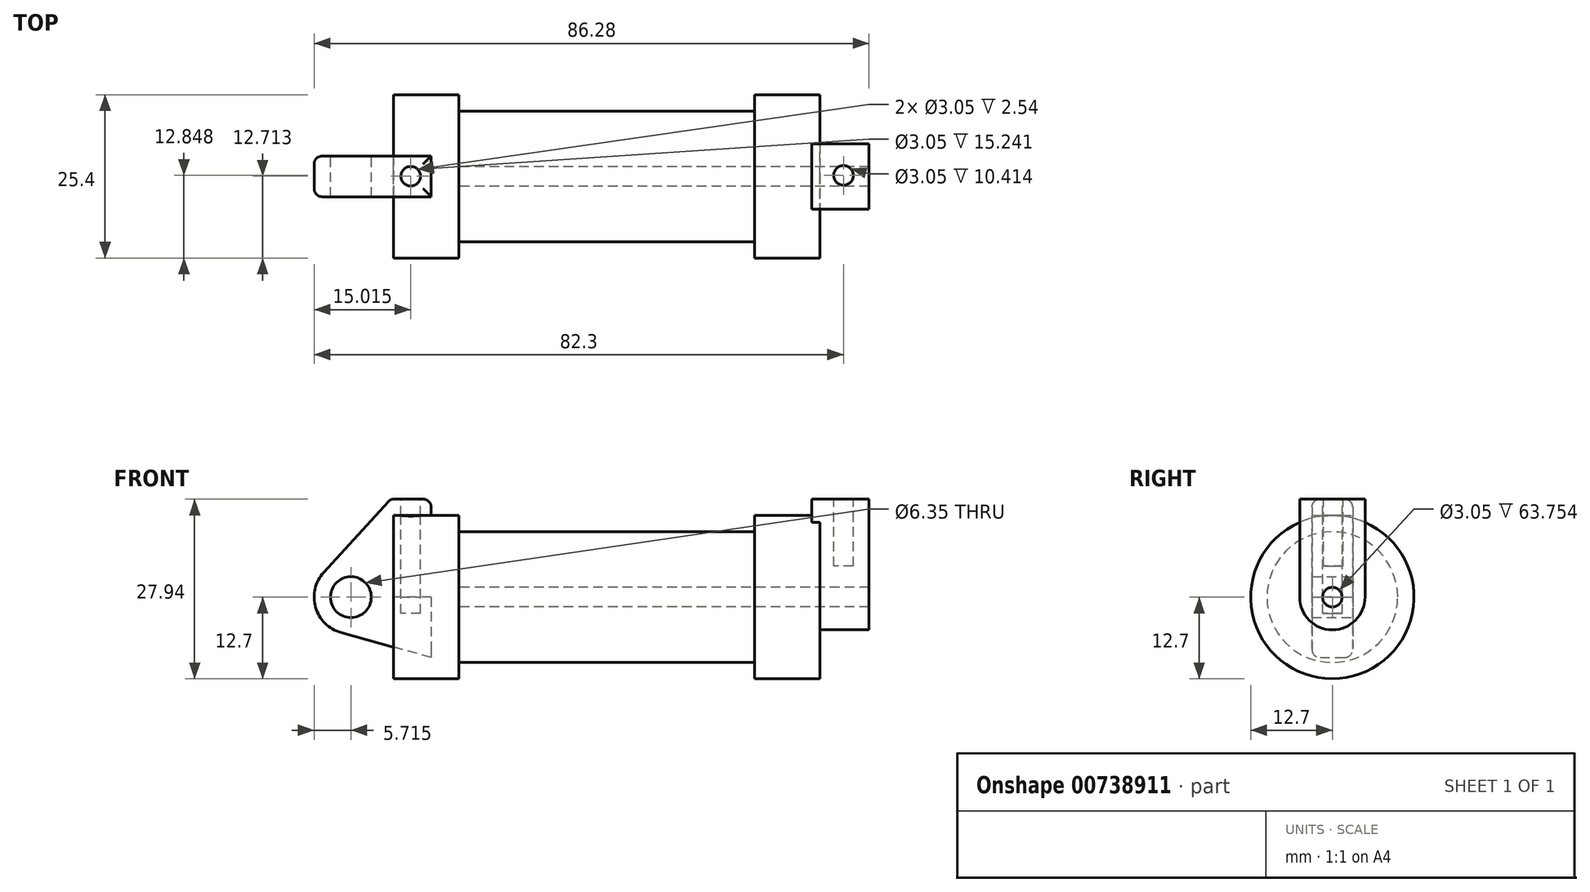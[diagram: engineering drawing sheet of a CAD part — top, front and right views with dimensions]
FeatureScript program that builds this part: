
annotation { "Feature Type Name" : "Feature", "Feature Type Description" : "" }
export const myFeature = defineFeature(function(context is Context, id is Id, definition is map)
    precondition{}
    {
        {
            var Q0;
            Q0=qCreatedBy(makeId("Front.planeOp"),FACE);
            var sketch = newSketch(context, id + "F0", { "sketchPlane" : qUnion([Q0])});
            skLineSegment(sketch, "E0", {"start": v(0, 0) * mm, "end": v(0, 12.7) * mm});
            skLineSegment(sketch, "E1", {"start": v(0, 12.7) * mm, "end": v(10.16, 12.7) * mm});
            skLineSegment(sketch, "E2", {"start": v(10.16, 12.7) * mm, "end": v(10.16, 10.16) * mm});
            skLineSegment(sketch, "E3", {"start": v(10.16, 10.16) * mm, "end": v(56.13, 10.16) * mm});
            skLineSegment(sketch, "E4", {"start": v(56.13, 10.16) * mm, "end": v(56.13, 12.7) * mm});
            skLineSegment(sketch, "E5", {"start": v(56.13, 12.7) * mm, "end": v(66.3, 12.7) * mm});
            skLineSegment(sketch, "E6", {"start": v(66.3, 12.7) * mm, "end": v(66.3, 0) * mm});
            skLineSegment(sketch, "E7", {"start": v(66.3, 0) * mm, "end": v(0, 0) * mm});
            skLineSegment(sketch, "E8", {"start": v(5.84, 15.24) * mm, "end": v(-0.5, 15.24) * mm});
            skLineSegment(sketch, "E9", {"start": v(-0.5, 15.24) * mm, "end": v(-10.88, 3.85) * mm});
            skLineSegment(sketch, "E10", {"start": v(0, 0) * mm, "end": v(-6.65, 0) * mm});
            skCircle(sketch, "E11", {"center": v(-6.65, 0) * mm, "radius": 5.72 * mm});
            skCircle(sketch, "E12", {"center": v(-6.65, 0) * mm, "radius": 3.18 * mm});
            skLineSegment(sketch, "E13", {"start": v(5.84, 15.24) * mm, "end": v(5.84, -9.4) * mm});
            skLineSegment(sketch, "E14", {"start": v(5.84, -9.4) * mm, "end": v(-8.18, -5.5) * mm});
            skSolve(sketch);
        }
        {
            var Q0;
            {var subQ0=sQuery(id+"F0.wireOp",EDGE,"E2");Q0=makeQuery(id+"F0.imprint","IMPRINT",FACE,{"disambiguationData":[TD([[makeQuery(id+"F0.imprint","IMPRINT",EDGE,{"derivedFrom":subQ0}),-1.0]])]});}
            var Q1;
            {var subQ0=sQuery(id+"F0.wireOp",EDGE,"E0");Q1=makeQuery(id+"F0.imprint","IMPRINT",FACE,{"disambiguationData":[TD([[makeQuery(id+"F0.imprint","IMPRINT",EDGE,{"derivedFrom":subQ0}),-1.0]])]});}
            var Q2;
            Q2=sQuery(id+"F0.wireOp",EDGE,"E7");
            revolve(context, id + "F1", {"surfaceOperationType" : NewSurfaceOperationType.NEW, "entities" : qUnion([Q0, Q1]), "axis" : qUnion([Q2]), "revolveType" : RevolveType.FULL});
        }
        {
            var Q0;
            {var subQ1=sQuery(id+"F0.wireOp",EDGE,"E0");Q0=makeQuery(id+"F0.imprint","IMPRINT",FACE,{"disambiguationData":[TD([[makeQuery(id+"F0.imprint","IMPRINT",EDGE,{"derivedFrom":subQ1}),1.0]])]});}
            var Q1;
            {var subQ5=sQuery(id+"F0.wireOp",EDGE,"E12");Q1=makeQuery(id+"F0.imprint","IMPRINT",FACE,{"disambiguationData":[TD([[makeQuery(id+"F0.imprint","IMPRINT",EDGE,{"derivedFrom":subQ5}),-1.0]])]});}
            var Q2;
            {var subQ0=sQuery(id+"F0.wireOp",EDGE,"E14");Q2=makeQuery(id+"F0.imprint","IMPRINT",FACE,{"disambiguationData":[TD([[makeQuery(id+"F0.imprint","IMPRINT",EDGE,{"derivedFrom":subQ0}),-1.0]])]});}
            extrude(context, id + "F2", {"entities" : qUnion([Q0, Q1, Q2]), "endBound" : BoundingType.SYMMETRIC, "depth" : 6.35 * mm, "offsetDistance" : 25.4 * mm});
        }
        {
            var Q0;
            Q0=makeQuery(id+"F1.opRevolve","SWEPT_FACE",FACE,{"disambiguationData":[OSD([sQuery(id+"F0.wireOp",EDGE,"E6")])]});
            var sketch = newSketch(context, id + "F3", { "sketchPlane" : qUnion([Q0])});
            skCircle(sketch, "E15", {"center": v(0, 0) * mm, "radius": 1.52 * mm});
            skCircle(sketch, "E16", {"center": v(0, 0) * mm, "radius": 5.08 * mm});
            skLineSegment(sketch, "E17", {"start": v(-5.08, 0) * mm, "end": v(-5.08, 15.24) * mm});
            skLineSegment(sketch, "E18", {"start": v(5.08, 0) * mm, "end": v(5.08, 15.24) * mm});
            skLineSegment(sketch, "E19", {"start": v(-5.08, 15.24) * mm, "end": v(5.08, 15.24) * mm});
            skSolve(sketch);
        }
        {
            var Q0;
            Q0 = qSketchRegion(id + "F3", true);
            var Q1;
            Q1=sQuery(id+"F3.wireOp",EDGE,"E16");
            var Q2;
            Q2=sQuery(id+"F3.wireOp",EDGE,"E17");
            var Q3;
            Q3=sQuery(id+"F3.wireOp",EDGE,"E15");
            var Q4;
            Q4=sQuery(id+"F3.wireOp",EDGE,"E18");
            var Q5;
            Q5=sQuery(id+"F3.wireOp",EDGE,"E19");
            extrude(context, id + "F4", {"entities" : qUnion([Q0]), "operationType" : NewBodyOperationType.ADD, "surfaceEntities" : qUnion([Q1, Q2, Q3, Q4, Q5]), "depth" : 7.62 * mm, "offsetDistance" : 25.4 * mm, "hasSecondDirection" : true, "secondDirectionOppositeDirection" : true, "secondDirectionDepth" : 1.27 * mm});
        }
        {
            var Q0;
            Q0=makeQuery(id+"F4.boolean.opBoolean","SPLIT",FACE,{"disambiguationData":[TD([makeQuery(id+"F4.opExtrude","SWEPT_FACE",FACE,{"disambiguationData":[OSD([sQuery(id+"F3.wireOp",EDGE,"E15")])]})])],"derivedFrom":makeQuery(id+"F1.opRevolve","SWEPT_FACE",FACE,{"disambiguationData":[OSD([sQuery(id+"F0.wireOp",EDGE,"E6")])]})});
            var Q1;
            Q1=makeQuery(id+"F1.opRevolve","SWEPT_FACE",FACE,{"disambiguationData":[OSD([sQuery(id+"F0.wireOp",EDGE,"E2")])]});
            extrude(context, id + "F5", {"entities" : qUnion([Q0]), "operationType" : NewBodyOperationType.REMOVE, "endBound" : BoundingType.UP_TO_SURFACE, "oppositeDirection" : true, "depth" : 25.4 * mm, "endBoundEntityFace" : qUnion([Q1]), "offsetDistance" : 25.4 * mm});
        }
        {
            var Q0;
            Q0=makeQuery(id+"F2.opExtrude","SWEPT_FACE",FACE,{"disambiguationData":[OSD([sQuery(id+"F0.wireOp",EDGE,"E8")])]});
            var sketch = newSketch(context, id + "F6", { "sketchPlane" : qUnion([Q0])});
            skCircle(sketch, "E20", {"center": v(2.65, 0.01) * mm, "radius": 1.52 * mm});
            skSolve(sketch);
        }
        {
            var Q0;
            Q0 = qSketchRegion(id + "F6", true);
            var Q1;
            Q1 = qSketchRegion(id + "F8", true);
            extrude(context, id + "F7", {"entities" : qUnion([Q0, Q1]), "operationType" : NewBodyOperationType.REMOVE, "oppositeDirection" : true, "depth" : 17.78 * mm, "offsetDistance" : 25.4 * mm});
        }
        {
            var Q0;
            Q0=makeQuery(id+"F4.opExtrude","SWEPT_FACE",FACE,{"disambiguationData":[OSD([sQuery(id+"F3.wireOp",EDGE,"E19")])]});
            var sketch = newSketch(context, id + "F8", { "sketchPlane" : qUnion([Q0])});
            skCircle(sketch, "E21", {"center": v(69.93, 0.15) * mm, "radius": 1.52 * mm});
            skSolve(sketch);
        }
        {
            var Q0;
            Q0 = qSketchRegion(id + "F8", true);
            extrude(context, id + "F9", {"entities" : qUnion([Q0]), "operationType" : NewBodyOperationType.REMOVE, "oppositeDirection" : true, "depth" : 10.4 * mm, "offsetDistance" : 25.4 * mm});
        }
        {
            var Q0;
            Q0=makeQuery(id+"F4.opExtrude","SWEPT_EDGE",EDGE,{"disambiguationData":[OSD([sQuery(id+"F3.wireOp",EDGE,"E17"),sQuery(id+"F3.wireOp",EDGE,"E19")])]});
            var Q1;
            Q1=makeQuery(id+"F4.opExtrude","CAP_EDGE",EDGE,{"disambiguationData":[OSD([sQuery(id+"F3.wireOp",EDGE,"E19")])],"isStart":false});
            var Q2;
            Q2=makeQuery(id+"F4.opExtrude","SWEPT_EDGE",EDGE,{"disambiguationData":[OSD([sQuery(id+"F3.wireOp",EDGE,"E18"),sQuery(id+"F3.wireOp",EDGE,"E19")])]});
            var Q3;
            Q3=makeQuery(id+"F4.opExtrude","CAP_EDGE",EDGE,{"disambiguationData":[OSD([sQuery(id+"F3.wireOp",EDGE,"E19")])],"isStart":true});
            var Q4;
            Q4=makeQuery(id+"F4.boolean.opBoolean","INTERSECT",EDGE,{"derivedFrom":[makeQuery(id+"F1.opRevolve","SWEPT_FACE",FACE,{"disambiguationData":[OSD([sQuery(id+"F0.wireOp",EDGE,"E6")])]}),makeQuery(id+"F4.opExtrude","SWEPT_FACE",FACE,{"disambiguationData":[OSD([sQuery(id+"F3.wireOp",EDGE,"E17")])]})]});
            var Q5;
            Q5=makeQuery(id+"F4.opExtrude","CAP_FACE",FACE,{"disambiguationData":[OSD([sQuery(id+"F3.wireOp",EDGE,"E15"),sQuery(id+"F3.wireOp",EDGE,"E16"),sQuery(id+"F3.wireOp",EDGE,"E17"),sQuery(id+"F3.wireOp",EDGE,"E18"),sQuery(id+"F3.wireOp",EDGE,"E19")])],"isStart":false});
            var Q6;
            Q6=makeQuery(id+"F1.opRevolve","SWEPT_EDGE",EDGE,{"disambiguationData":[OSD([sQuery(id+"F0.wireOp",EDGE,"E5"),sQuery(id+"F0.wireOp",EDGE,"E6")])]});
            var Q7;
            Q7=makeQuery(id+"F1.opRevolve","SWEPT_EDGE",EDGE,{"disambiguationData":[OSD([sQuery(id+"F0.wireOp",EDGE,"E4"),sQuery(id+"F0.wireOp",EDGE,"E5")])]});
            var Q8;
            Q8=makeQuery(id+"F1.opRevolve","SWEPT_EDGE",EDGE,{"disambiguationData":[OSD([sQuery(id+"F0.wireOp",EDGE,"E3"),sQuery(id+"F0.wireOp",EDGE,"E4")])]});
            var Q9;
            Q9=makeQuery(id+"F2.opExtrude","SWEPT_EDGE",EDGE,{"disambiguationData":[OSD([sQuery(id+"F0.wireOp",EDGE,"E8"),sQuery(id+"F0.wireOp",EDGE,"E9")])]});
            var Q10;
            Q10=makeQuery(id+"F2.opExtrude","SWEPT_EDGE",EDGE,{"disambiguationData":[OSD([sQuery(id+"F0.wireOp",EDGE,"E8"),sQuery(id+"F0.wireOp",EDGE,"E13")])]});
            var Q11;
            Q11=makeQuery(id+"F2.opExtrude","CAP_EDGE",EDGE,{"disambiguationData":[OSD([sQuery(id+"F0.wireOp",EDGE,"E8")])],"isStart":false});
            var Q12;
            Q12=makeQuery(id+"F2.opExtrude","CAP_EDGE",EDGE,{"disambiguationData":[OSD([sQuery(id+"F0.wireOp",EDGE,"E8")])],"isStart":true});
            var Q13;
            Q13=makeQuery(id+"F1.opRevolve","SWEPT_EDGE",EDGE,{"disambiguationData":[OSD([sQuery(id+"F0.wireOp",EDGE,"E0"),sQuery(id+"F0.wireOp",EDGE,"E1")])]});
            var Q14;
            Q14=makeQuery(id+"F2.opExtrude","CAP_EDGE",EDGE,{"disambiguationData":[OSD([sQuery(id+"F0.wireOp",EDGE,"E9")])],"isStart":true});
            var Q15;
            Q15=makeQuery(id+"F2.opExtrude","CAP_EDGE",EDGE,{"disambiguationData":[OSD([sQuery(id+"F0.wireOp",EDGE,"E11")])],"isStart":false});
            var Q16;
            Q16=makeQuery(id+"F1.opRevolve","SWEPT_EDGE",EDGE,{"disambiguationData":[OSD([sQuery(id+"F0.wireOp",EDGE,"E1"),sQuery(id+"F0.wireOp",EDGE,"E2")])]});
            var Q17;
            Q17=makeQuery(id+"F1.opRevolve","SWEPT_EDGE",EDGE,{"disambiguationData":[OSD([sQuery(id+"F0.wireOp",EDGE,"E2"),sQuery(id+"F0.wireOp",EDGE,"E3")])]});
            fillet(context, id + "F10", {"entities" : qUnion([Q0, Q1, Q2, Q3, Q4, Q5, Q6, Q7, Q8, Q9, Q10, Q11, Q12, Q13, Q14, Q15, Q16, Q17]), "radius" : 1.27 * mm, "tangentPropagation" : true, "allowEdgeOverflow" : false});
        }
    });
